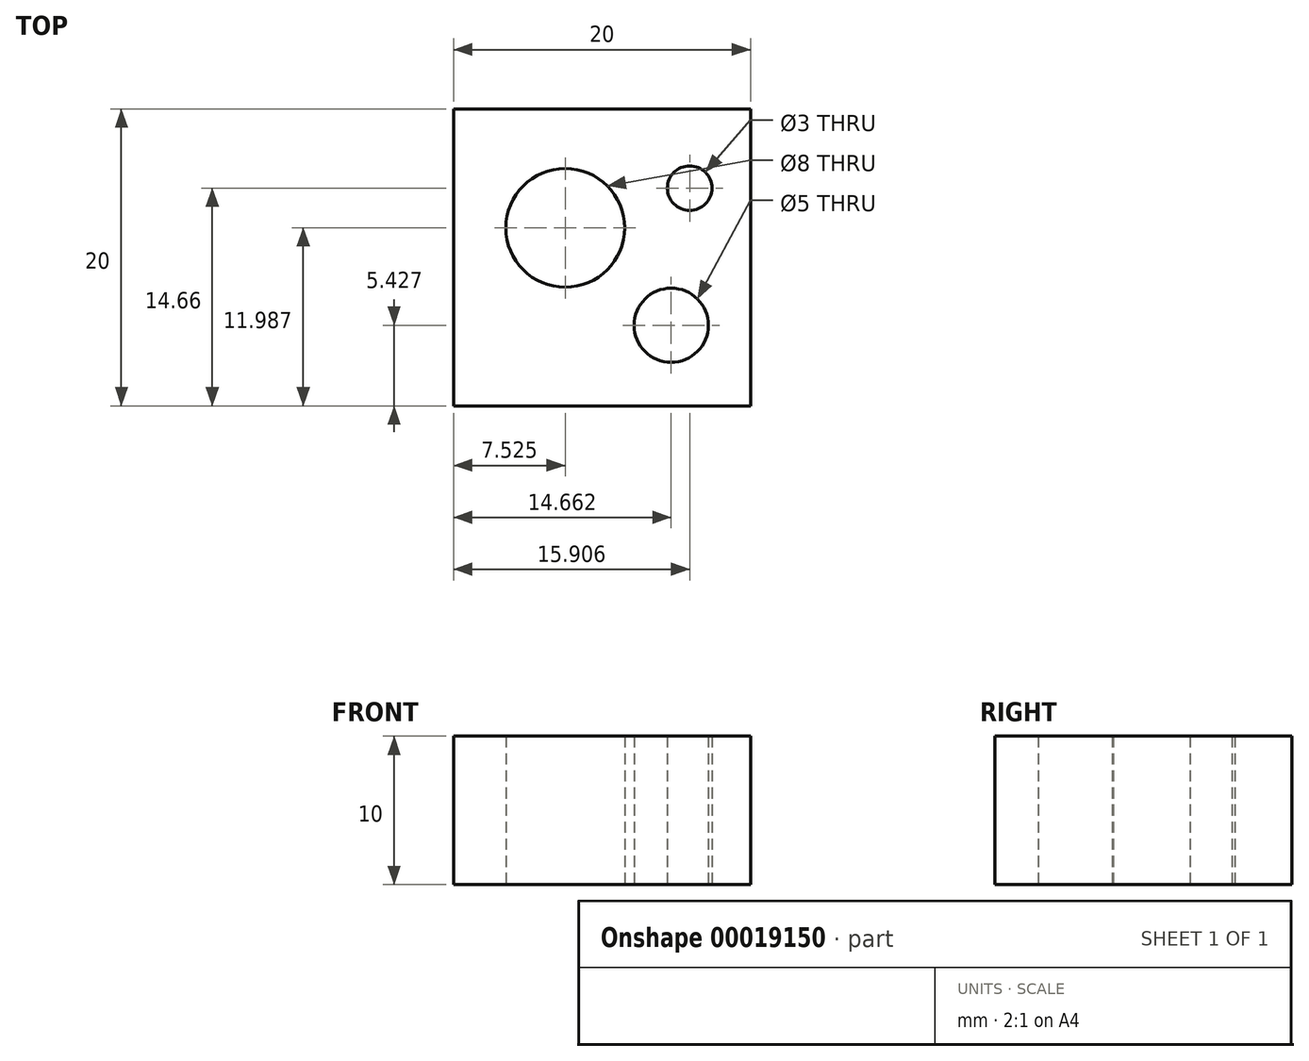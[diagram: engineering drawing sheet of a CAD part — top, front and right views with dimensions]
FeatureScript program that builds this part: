
annotation { "Feature Type Name" : "Feature", "Feature Type Description" : "" }
export const myFeature = defineFeature(function(context is Context, id is Id, definition is map)
    precondition{}
    {
        {
            var Q0;
            Q0=qCreatedBy(makeId("Top.planeOp"),FACE);
            var sketch = newSketch(context, id + "F0", { "sketchPlane" : qUnion([Q0])});
            skCircle(sketch, "E0", {"center": v(0, 0) * mm, "radius": 30 * mm});
            skCircle(sketch, "E1", {"center": v(-108.66, 0) * mm, "radius": 30 * mm});
            skCircle(sketch, "E2", {"center": v(-58.08, -65.99) * mm, "radius": 12.5 * mm});
            skSolve(sketch);
        }
        {
            var Q0;
            Q0=makeQuery(id+"F0.imprint","IMPRINT",FACE,{"disambiguationData":[TD([[makeQuery(id+"F0.imprint","IMPRINT",EDGE,{"derivedFrom":sQuery(id+"F0.wireOp",EDGE,"E1")}),1.0]])]});
            var Q1;
            Q1=makeQuery(id+"F0.imprint","IMPRINT",FACE,{"disambiguationData":[TD([[makeQuery(id+"F0.imprint","IMPRINT",EDGE,{"derivedFrom":sQuery(id+"F0.wireOp",EDGE,"E0")}),1.0]])]});
            extrude(context, id + "F1", {"entities" : qUnion([Q0, Q1]), "depth" : 15 * mm});
        }
        {
            var Q0;
            Q0=qCreatedBy(makeId("Top.planeOp"),FACE);
            var sketch = newSketch(context, id + "F2", { "sketchPlane" : qUnion([Q0])});
            skCircle(sketch, "E3", {"center": v(-60.96, -55.41) * mm, "radius": 12.5 * mm});
            skSolve(sketch);
        }
        {
            var Q0;
            Q0=makeQuery(id+"F2.imprint","IMPRINT",FACE,{"disambiguationData":[TD([[makeQuery(id+"F2.imprint","IMPRINT",EDGE,{"derivedFrom":sQuery(id+"F2.wireOp",EDGE,"E3")}),1.0]])]});
            extrude(context, id + "F3", {"entities" : qUnion([Q0]), "depth" : 35 * mm});
        }
        {
            var Q0;
            Q0=makeQuery(id+"F1.opExtrude","SWEPT_BODY",BODY,{"disambiguationData":[OSD([sQuery(id+"F0.wireOp",EDGE,"E0")])]});
            var Q1;
            Q1=makeQuery(id+"F1.opExtrude","SWEPT_BODY",BODY,{"disambiguationData":[OSD([sQuery(id+"F0.wireOp",EDGE,"E1")])]});
            var Q2;
            Q2=makeQuery(id+"F3.opExtrude","SWEPT_BODY",BODY,{"disambiguationData":[OSD([sQuery(id+"F2.wireOp",EDGE,"E3")])]});
            deleteBodies(context, id + "F4", {"entities" : qUnion([Q0, Q1, Q2])});
        }
        {
            var Q0;
            Q0=qCreatedBy(makeId("Top.planeOp"),FACE);
            var sketch = newSketch(context, id + "F5", { "sketchPlane" : qUnion([Q0])});
            skLineSegment(sketch, "E4.rect.bottom", {"start": v(10, -10) * mm, "end": v(-10, -10) * mm});
            skLineSegment(sketch, "E4.rect.top", {"start": v(10, 10) * mm, "end": v(-10, 10) * mm});
            skLineSegment(sketch, "E4.rect.left", {"start": v(10, -10) * mm, "end": v(10, 10) * mm});
            skLineSegment(sketch, "E4.rect.right", {"start": v(-10, -10) * mm, "end": v(-10, 10) * mm});
            skPoint(sketch, "E4.rect.middle", {"position": v(0, 0) * mm});
            skCircle(sketch, "E5", {"center": v(5.9, 4.66) * mm, "radius": 1.5 * mm});
            skCircle(sketch, "E6", {"center": v(-2.47, 1.99) * mm, "radius": 4 * mm});
            skCircle(sketch, "E7", {"center": v(4.66, -4.57) * mm, "radius": 2.5 * mm});
            skSolve(sketch);
        }
        {
            var Q0;
            Q0=makeQuery(id+"F5.imprint","IMPRINT",FACE,{"disambiguationData":[TD([[makeQuery(id+"F5.imprint","IMPRINT",EDGE,{"derivedFrom":sQuery(id+"F5.wireOp",EDGE,"E4.rect.bottom")}),-1.0]])]});
            extrude(context, id + "F6", {"entities" : qUnion([Q0]), "depth" : 10 * mm});
        }
    });
